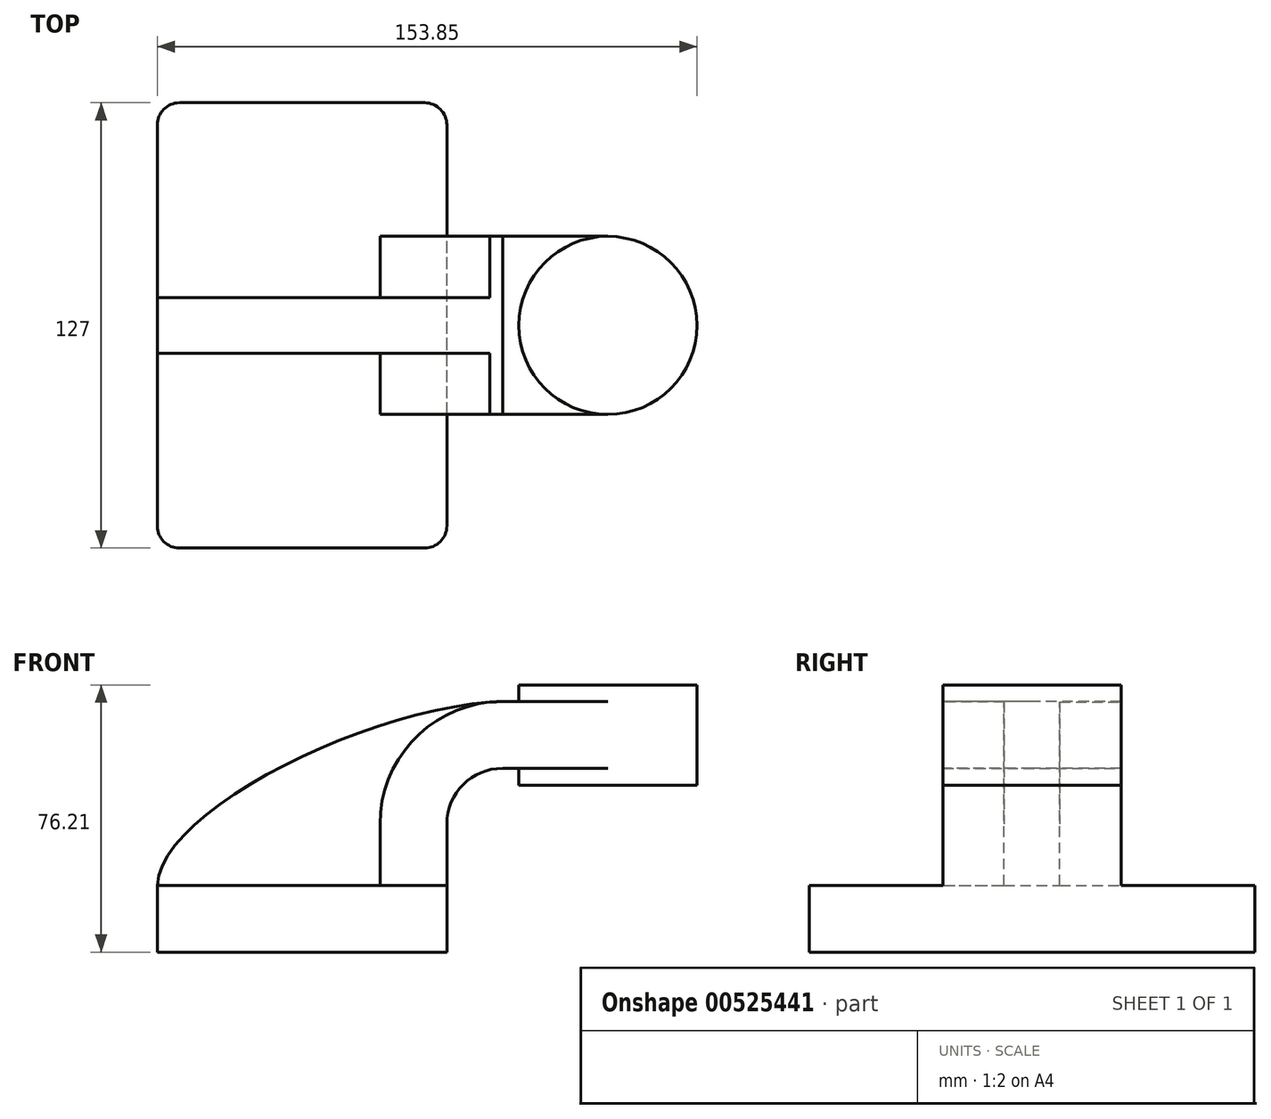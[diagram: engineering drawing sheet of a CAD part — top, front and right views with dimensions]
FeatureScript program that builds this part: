
annotation { "Feature Type Name" : "Feature", "Feature Type Description" : "" }
export const myFeature = defineFeature(function(context is Context, id is Id, definition is map)
    precondition{}
    {
        {
            var Q0;
            Q0=qCreatedBy(makeId("Front.planeOp"),FACE);
            var sketch = newSketch(context, id + "F0", { "sketchPlane" : qUnion([Q0])});
            skLineSegment(sketch, "E0.bottom", {"start": v(-41.28, 9.52) * mm, "end": v(41.27, 9.53) * mm});
            skLineSegment(sketch, "E0.top", {"start": v(-41.28, -9.53) * mm, "end": v(41.28, -9.53) * mm});
            skLineSegment(sketch, "E0.left", {"start": v(-41.28, 9.52) * mm, "end": v(-41.28, -9.53) * mm});
            skLineSegment(sketch, "E0.right", {"start": v(41.27, 9.53) * mm, "end": v(41.28, -9.52) * mm});
            skPoint(sketch, "E0.middle", {"position": v(0, 0) * mm});
            skLineSegment(sketch, "E1.bottom", {"start": v(61.77, 38.1) * mm, "end": v(112.57, 38.1) * mm});
            skLineSegment(sketch, "E1.top", {"start": v(61.77, 66.68) * mm, "end": v(112.57, 66.68) * mm});
            skLineSegment(sketch, "E1.left", {"start": v(61.77, 38.1) * mm, "end": v(61.77, 66.68) * mm});
            skLineSegment(sketch, "E1.right", {"start": v(112.57, 38.1) * mm, "end": v(112.57, 66.68) * mm});
            skPoint(sketch, "E1.middle", {"position": v(87.17, 52.39) * mm});
            skLineSegment(sketch, "E2", {"start": v(41.27, 9.53) * mm, "end": v(41.27, 27) * mm});
            skArc(sketch, "E3", {"start": v(41.27, 27) * mm, "mid": v(45.92, 38.23) * mm, "end": v(57.15, 42.88) * mm});
            skLineSegment(sketch, "E4", {"start": v(57.15, 42.88) * mm, "end": v(87.17, 42.88) * mm});
            skLineSegment(sketch, "E5.0", {"start": v(57.15, 61.93) * mm, "end": v(87.17, 61.93) * mm});
            skArc(sketch, "E5.1", {"start": v(22.22, 27) * mm, "mid": v(32.45, 51.7) * mm, "end": v(57.15, 61.93) * mm});
            skLineSegment(sketch, "E5.2", {"start": v(22.22, 9.53) * mm, "end": v(22.22, 27) * mm});
            skLineSegment(sketch, "E6", {"start": v(87.17, 38.1) * mm, "end": v(87.17, 66.68) * mm});
            skFitSpline(sketch, "E7", {"points": [v(-41.28, 9.52) * mm, v(57.15, 61.93) * mm], "startDerivative": vector(2.25, 64.34) * mm, "endDerivative": vector(112.18, 3.26) * mm});
            skSolve(sketch);
        }
        {
            var Q0;
            Q0=makeQuery(id+"F0.imprint","IMPRINT",FACE,{"disambiguationData":[TD([[makeQuery(id+"F0.imprint","IMPRINT",EDGE,{"derivedFrom":sQuery(id+"F0.wireOp",EDGE,"E0.top")}),1.0]])]});
            extrude(context, id + "F1", {"entities" : qUnion([Q0]), "endBound" : BoundingType.SYMMETRIC, "depth" : 127 * mm, "offsetDistance" : 25.4 * mm});
        }
        {
            var Q0;
            {var subQ1=sQuery(id+"F0.wireOp",EDGE,"E2");Q0=makeQuery(id+"F0.imprint","IMPRINT",FACE,{"disambiguationData":[TD([[makeQuery(id+"F0.imprint","IMPRINT",EDGE,{"derivedFrom":subQ1}),1.0]])]});}
            var Q1;
            {var subQ0=sQuery(id+"F0.wireOp",EDGE,"E4");var subQ1=sQuery(id+"F0.wireOp",EDGE,"E1.left");var subQ2=makeQuery(id+"F0.imprint","INTERSECT",VERTEX,{"derivedFrom":[subQ1,subQ0]});Q1=makeQuery(id+"F0.imprint","IMPRINT",FACE,{"disambiguationData":[TD([[makeQuery(id+"F0.imprint","IMPRINT",EDGE,{"disambiguationData":[TD([[subQ2,-1.0]])],"derivedFrom":subQ1}),-1.0]])]});}
            extrude(context, id + "F2", {"entities" : qUnion([Q0, Q1]), "operationType" : NewBodyOperationType.ADD, "endBound" : BoundingType.SYMMETRIC, "depth" : 50.8 * mm, "offsetDistance" : 25.4 * mm});
        }
        {
            var Q0;
            {var subQ3=sQuery(id+"F0.wireOp",EDGE,"E5.2");Q0=makeQuery(id+"F0.imprint","IMPRINT",FACE,{"disambiguationData":[TD([[makeQuery(id+"F0.imprint","IMPRINT",EDGE,{"derivedFrom":subQ3}),1.0]])]});}
            extrude(context, id + "F3", {"entities" : qUnion([Q0]), "operationType" : NewBodyOperationType.ADD, "endBound" : BoundingType.SYMMETRIC, "depth" : 15.88 * mm, "offsetDistance" : 25.4 * mm});
        }
        {
            var Q0;
            {var subQ4=sQuery(id+"F0.wireOp",EDGE,"E1.right");Q0=makeQuery(id+"F0.imprint","IMPRINT",FACE,{"disambiguationData":[TD([[makeQuery(id+"F0.imprint","IMPRINT",EDGE,{"derivedFrom":subQ4}),1.0]])]});}
            var Q1;
            Q1=sQuery(id+"F0.wireOp",EDGE,"E6");
            revolve(context, id + "F4", {"operationType" : NewBodyOperationType.ADD, "entities" : qUnion([Q0]), "axis" : qUnion([Q1]), "revolveType" : RevolveType.FULL});
        }
        {
            var Q0;
            Q0=makeQuery(id+"F1.opExtrude","CAP_EDGE",EDGE,{"disambiguationData":[OSD([sQuery(id+"F0.wireOp",EDGE,"E0.right")])],"isStart":false});
            var Q1;
            Q1=makeQuery(id+"F1.opExtrude","CAP_EDGE",EDGE,{"disambiguationData":[OSD([sQuery(id+"F0.wireOp",EDGE,"E0.left")])],"isStart":false});
            var Q2;
            Q2=makeQuery(id+"F1.opExtrude","CAP_EDGE",EDGE,{"disambiguationData":[OSD([sQuery(id+"F0.wireOp",EDGE,"E0.right")])],"isStart":true});
            var Q3;
            Q3=makeQuery(id+"F1.opExtrude","CAP_EDGE",EDGE,{"disambiguationData":[OSD([sQuery(id+"F0.wireOp",EDGE,"E0.left")])],"isStart":true});
            fillet(context, id + "F5", {"entities" : qUnion([Q0, Q1, Q2, Q3]), "radius" : 6.35 * mm, "tangentPropagation" : true, "allowEdgeOverflow" : false});
        }
    });
